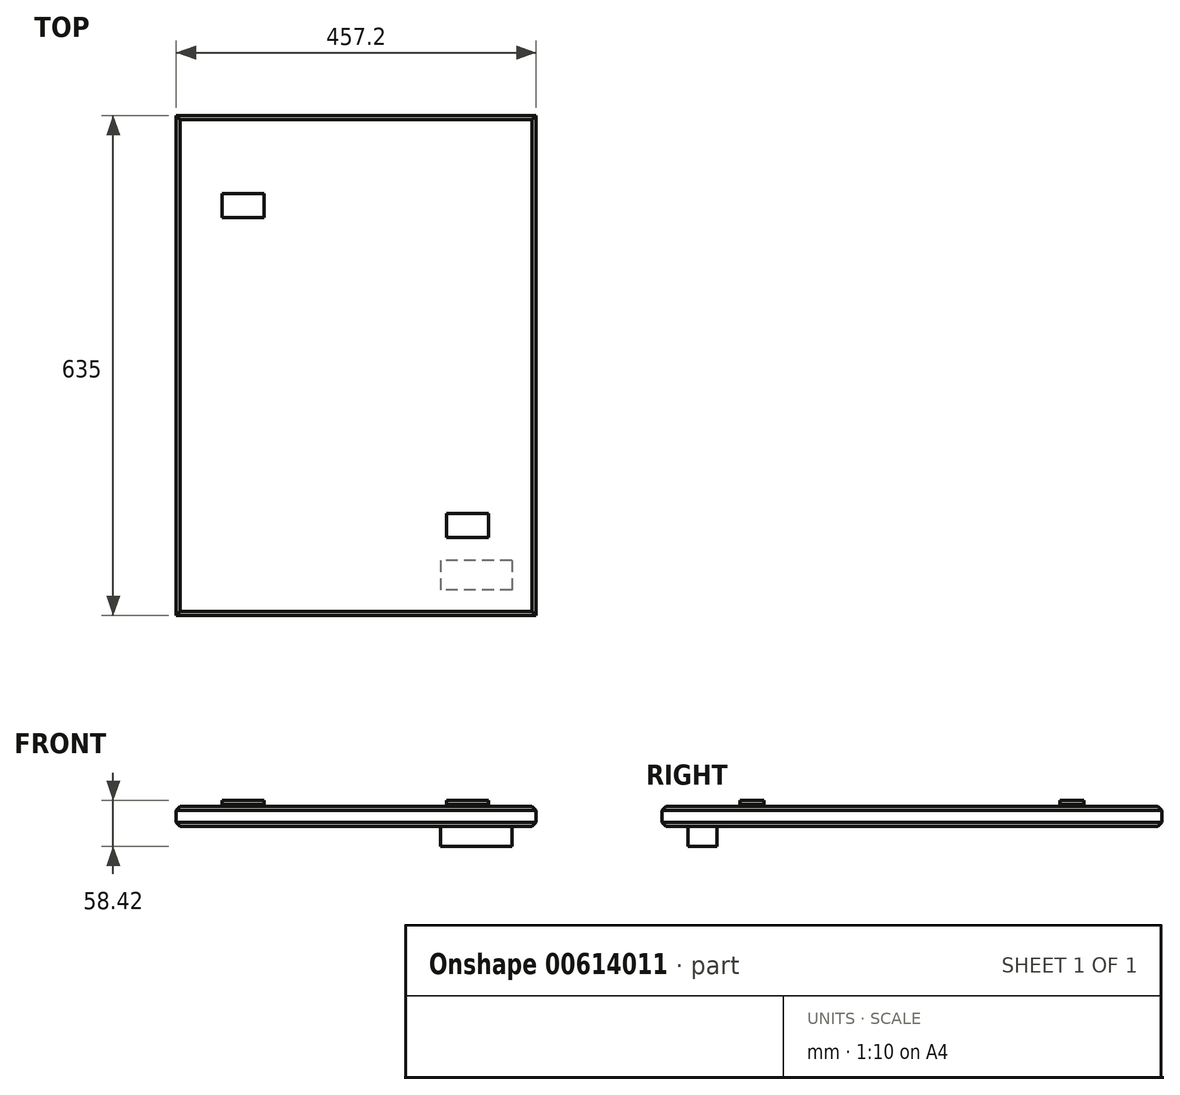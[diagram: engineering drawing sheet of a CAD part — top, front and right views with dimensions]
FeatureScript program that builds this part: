
annotation { "Feature Type Name" : "Feature", "Feature Type Description" : "" }
export const myFeature = defineFeature(function(context is Context, id is Id, definition is map)
    precondition{}
    {
        {
            var Q0;
            Q0=qCreatedBy(makeId("Top.planeOp"),FACE);
            var sketch = newSketch(context, id + "F0", { "sketchPlane" : qUnion([Q0])});
            skLineSegment(sketch, "E0.bottom", {"start": v(-228.6, 317.5) * mm, "end": v(228.6, 317.5) * mm});
            skLineSegment(sketch, "E0.top", {"start": v(-228.6, -317.5) * mm, "end": v(228.6, -317.5) * mm});
            skLineSegment(sketch, "E0.left", {"start": v(-228.6, 317.5) * mm, "end": v(-228.6, -317.5) * mm});
            skLineSegment(sketch, "E0.right", {"start": v(228.6, 317.5) * mm, "end": v(228.6, -317.5) * mm});
            skPoint(sketch, "E0.middle", {"position": v(0, 0) * mm});
            skSolve(sketch);
        }
        {
            var Q0;
            Q0=qSketchRegion(id+"F0",true);
            extrude(context, id + "F1", {"entities" : qUnion([Q0]), "depth" : 25.4 * mm, "offsetDistance" : 25.4 * mm});
        }
        {
            var Q0;
            Q0=makeQuery(id+"F1.opExtrude","CAP_EDGE",EDGE,{"disambiguationData":[OSD([sQuery(id+"F0.wireOp",EDGE,"E0.top")])],"isStart":false});
            var Q1;
            Q1=makeQuery(id+"F1.opExtrude","CAP_EDGE",EDGE,{"disambiguationData":[OSD([sQuery(id+"F0.wireOp",EDGE,"E0.left")])],"isStart":false});
            var Q2;
            Q2=makeQuery(id+"F1.opExtrude","CAP_EDGE",EDGE,{"disambiguationData":[OSD([sQuery(id+"F0.wireOp",EDGE,"E0.bottom")])],"isStart":false});
            var Q3;
            Q3=makeQuery(id+"F1.opExtrude","CAP_EDGE",EDGE,{"disambiguationData":[OSD([sQuery(id+"F0.wireOp",EDGE,"E0.right")])],"isStart":false});
            var Q4;
            Q4=makeQuery(id+"F1.opExtrude","CAP_EDGE",EDGE,{"disambiguationData":[OSD([sQuery(id+"F0.wireOp",EDGE,"E0.right")])],"isStart":true});
            var Q5;
            Q5=makeQuery(id+"F1.opExtrude","CAP_EDGE",EDGE,{"disambiguationData":[OSD([sQuery(id+"F0.wireOp",EDGE,"E0.top")])],"isStart":true});
            var Q6;
            Q6=makeQuery(id+"F1.opExtrude","CAP_EDGE",EDGE,{"disambiguationData":[OSD([sQuery(id+"F0.wireOp",EDGE,"E0.left")])],"isStart":true});
            var Q7;
            Q7=makeQuery(id+"F1.opExtrude","CAP_EDGE",EDGE,{"disambiguationData":[OSD([sQuery(id+"F0.wireOp",EDGE,"E0.bottom")])],"isStart":true});
            chamfer(context, id + "F2", {"entities" : qUnion([Q0, Q1, Q2, Q3, Q4, Q5, Q6, Q7]), "width" : 5.08 * mm, "tangentPropagation" : true});
        }
        {
            var Q0;
            Q0=makeQuery(id+"F1.opExtrude","CAP_FACE",FACE,{"disambiguationData":[OSD([sQuery(id+"F0.wireOp",EDGE,"E0.bottom"),sQuery(id+"F0.wireOp",EDGE,"E0.top"),sQuery(id+"F0.wireOp",EDGE,"E0.left"),sQuery(id+"F0.wireOp",EDGE,"E0.right")])],"isStart":true});
            var sketch = newSketch(context, id + "F3", { "sketchPlane" : qUnion([Q0])});
            skLineSegment(sketch, "E1.bottom", {"start": v(197.87, 247.58) * mm, "end": v(107.2, 247.58) * mm});
            skLineSegment(sketch, "E1.top", {"start": v(197.87, 284.92) * mm, "end": v(107.2, 284.92) * mm});
            skLineSegment(sketch, "E1.left", {"start": v(197.87, 247.58) * mm, "end": v(197.87, 284.92) * mm});
            skLineSegment(sketch, "E1.right", {"start": v(107.2, 247.58) * mm, "end": v(107.2, 284.92) * mm});
            skSolve(sketch);
        }
        {
            var Q0;
            Q0=makeQuery(id+"F3.imprint","IMPRINT",FACE,{"disambiguationData":[TD([[makeQuery(id+"F3.imprint","IMPRINT",EDGE,{"derivedFrom":sQuery(id+"F3.wireOp",EDGE,"E1.bottom")}),-1.0]])]});
            extrude(context, id + "F4", {"entities" : qUnion([Q0]), "operationType" : NewBodyOperationType.ADD, "depth" : 25.4 * mm, "offsetDistance" : 25.4 * mm});
        }
        {
            var Q0;
            Q0=qCreatedBy(makeId("Top.planeOp"),FACE);
            var sketch = newSketch(context, id + "F5", { "sketchPlane" : qUnion([Q0])});
            skLineSegment(sketch, "E2.bottom", {"start": v(-698.37, 114.43) * mm, "end": v(-751.7, 114.43) * mm});
            skLineSegment(sketch, "E2.top", {"start": v(-698.37, 144.91) * mm, "end": v(-751.7, 144.91) * mm});
            skLineSegment(sketch, "E2.left", {"start": v(-698.37, 114.43) * mm, "end": v(-698.37, 144.91) * mm});
            skLineSegment(sketch, "E2.right", {"start": v(-751.7, 114.43) * mm, "end": v(-751.7, 144.91) * mm});
            skPoint(sketch, "E2.middle", {"position": v(-725.04, 129.67) * mm});
            skSolve(sketch);
        }
        {
            var Q0;
            Q0=qSketchRegion(id+"F5",true);
            extrude(context, id + "F6", {"entities" : qUnion([Q0]), "depth" : 5.08 * mm, "offsetDistance" : 25.4 * mm});
        }
        {
            var Q0;
            Q0=makeQuery(id+"F6.opExtrude","SWEPT_BODY",BODY,{"disambiguationData":[OSD([sQuery(id+"F5.wireOp",EDGE,"E2.bottom"),sQuery(id+"F5.wireOp",EDGE,"E2.top"),sQuery(id+"F5.wireOp",EDGE,"E2.left"),sQuery(id+"F5.wireOp",EDGE,"E2.right")])]});
            transform(context, id + "F7", {"entities" : qUnion([Q0]), "transformType" : TransformType.TRANSLATION_3D, "dx" : 0 * mm, "dy" : 203.2 * mm, "dz" : 0 * mm, "makeCopy" : true});
        }
        {
            var Q0;
            Q0=makeQuery(id+"F6.opExtrude","SWEPT_BODY",BODY,{"disambiguationData":[OSD([sQuery(id+"F5.wireOp",EDGE,"E2.bottom"),sQuery(id+"F5.wireOp",EDGE,"E2.top"),sQuery(id+"F5.wireOp",EDGE,"E2.left"),sQuery(id+"F5.wireOp",EDGE,"E2.right")])]});
            transform(context, id + "F8", {"entities" : qUnion([Q0]), "transformType" : TransformType.TRANSLATION_3D, "dx" : 0 * mm, "dy" : -203.2 * mm, "dz" : 0 * mm, "makeCopy" : true});
        }
        {
            var Q0;
            Q0=makeQuery(id+"F8.opPattern","COPY",BODY,{"derivedFrom":makeQuery(id+"F6.opExtrude","SWEPT_BODY",BODY,{"disambiguationData":[OSD([sQuery(id+"F5.wireOp",EDGE,"E2.bottom"),sQuery(id+"F5.wireOp",EDGE,"E2.top"),sQuery(id+"F5.wireOp",EDGE,"E2.left"),sQuery(id+"F5.wireOp",EDGE,"E2.right")])]}),"instanceName":"1"});
            var Q1;
            Q1=makeQuery(id+"F7.opPattern","COPY",BODY,{"derivedFrom":makeQuery(id+"F6.opExtrude","SWEPT_BODY",BODY,{"disambiguationData":[OSD([sQuery(id+"F5.wireOp",EDGE,"E2.bottom"),sQuery(id+"F5.wireOp",EDGE,"E2.top"),sQuery(id+"F5.wireOp",EDGE,"E2.left"),sQuery(id+"F5.wireOp",EDGE,"E2.right")])]}),"instanceName":"1"});
            var Q2;
            Q2=makeQuery(id+"F6.opExtrude","SWEPT_BODY",BODY,{"disambiguationData":[OSD([sQuery(id+"F5.wireOp",EDGE,"E2.bottom"),sQuery(id+"F5.wireOp",EDGE,"E2.top"),sQuery(id+"F5.wireOp",EDGE,"E2.left"),sQuery(id+"F5.wireOp",EDGE,"E2.right")])]});
            transform(context, id + "F9", {"entities" : qUnion([Q0, Q1, Q2]), "transformType" : TransformType.TRANSLATION_3D, "dx" : 723.9 * mm, "dy" : -129.54 * mm, "dz" : 27.94 * mm, "makeCopy" : false});
        }
        {
            var Q0;
            Q0=makeQuery(id+"F7.opPattern","COPY",BODY,{"derivedFrom":makeQuery(id+"F6.opExtrude","SWEPT_BODY",BODY,{"disambiguationData":[OSD([sQuery(id+"F5.wireOp",EDGE,"E2.bottom"),sQuery(id+"F5.wireOp",EDGE,"E2.top"),sQuery(id+"F5.wireOp",EDGE,"E2.left"),sQuery(id+"F5.wireOp",EDGE,"E2.right")])]}),"instanceName":"1"});
            transform(context, id + "F10", {"entities" : qUnion([Q0]), "transformType" : TransformType.TRANSLATION_3D, "dx" : -142.75 * mm, "dy" : 0 * mm, "dz" : 0 * mm, "makeCopy" : false});
        }
        {
            var Q0;
            Q0=makeQuery(id+"F8.opPattern","COPY",BODY,{"derivedFrom":makeQuery(id+"F6.opExtrude","SWEPT_BODY",BODY,{"disambiguationData":[OSD([sQuery(id+"F5.wireOp",EDGE,"E2.bottom"),sQuery(id+"F5.wireOp",EDGE,"E2.top"),sQuery(id+"F5.wireOp",EDGE,"E2.left"),sQuery(id+"F5.wireOp",EDGE,"E2.right")])]}),"instanceName":"1"});
            transform(context, id + "F11", {"entities" : qUnion([Q0]), "transformType" : TransformType.TRANSLATION_3D, "dx" : 142.75 * mm, "dy" : 0 * mm, "dz" : 0 * mm, "makeCopy" : false});
        }
        {
            var Q0;
            Q0=makeQuery(id+"F6.opExtrude","CAP_FACE",FACE,{"disambiguationData":[OSD([sQuery(id+"F5.wireOp",EDGE,"E2.bottom"),sQuery(id+"F5.wireOp",EDGE,"E2.top"),sQuery(id+"F5.wireOp",EDGE,"E2.left"),sQuery(id+"F5.wireOp",EDGE,"E2.right")])],"isStart":false});
            extrude(context, id + "F12", {"entities" : qUnion([Q0]), "operationType" : NewBodyOperationType.REMOVE, "oppositeDirection" : true, "depth" : 6.35 * mm, "offsetDistance" : 25.4 * mm});
        }
    });
